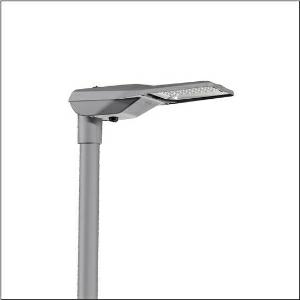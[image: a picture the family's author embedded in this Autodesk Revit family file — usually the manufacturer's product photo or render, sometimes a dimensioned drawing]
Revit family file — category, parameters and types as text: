
# Revit family: streetlight_sl_21_iq_mini___stw1_0a_5xe2e31y08hb_518f
name_source: partatom
category: Lighting Fixtures
units: mm (PartAtom-declared; Revit-internal decimal feet)

## family parameters
Cut with Voids When Loaded = No
Host = Face
Light Source = No
Part Type = Normal
Room Calculation Point = No
Round Connector Dimension = Use Diameter
Shared = No

## types (1)
- --- (1 x LED, 9750 lm, 71 W, 3000K)
    Apparent Load = 71 VA
    CIE Flux Codes = 38 75 98 100 100
    Color Rendering = 70
    Color Temperature = 3000K
    Default Elevation = 1800 mm
    Description = Streetlight SL 21 iQ mini, mast luminaire, primary light control with lens, of PMMA, primary optical cover: cover, of toughened safety glass, transparent, light distribution: STW1.0a, light emission: direct distribution, primary light characteristic: asymmetric, installation type: post-top, side-entry, LED, High Power LED, rated luminous flux: 9.750lm, luminous efficacy: 137lm/W, light colour: 730, colour temperature: 3000K, control gear: iQ-Street Remote, D4i with power reduction, control: pre-setting: logarithmic dimming characteristic, Street-Remote, Auto-Match, Temp-Guard, Lumen-Switch, Night-Set, Smart-Wire, Light-Fading, Desk-Remote (wireless, voltage-free reading and setting of iQ features in the workshop via application-optimized NFC function/RFID function), optimised constant luminous flux control (CLO 2.0), mains connection: 220..240V, AC, 50/60Hz, start of lifetime: 71W, end of service life: 75W, reduction: 30W, luminaire housing, of diecast aluminium, powder-coated, SITECO metallic grey (DB 702S), corrosivity category C5 high according to DIN EN ISO 12944, please order mast flange separately, inclination adjustable: 0°, 5°, 10°, 15°, sealing non-destructively replaceable, multi-level sealing system, length: 628mm, width: 235mm, height: 110mm, mast flange for spigot size: 42mm (side-entry): 5XC10008XM4, 60/48mm (side-entry/post-top): 5XC10108XM2, 76/60mm (side-entry/post-top): 5XC10108XM1, mounting height: 4..8m, Smart Interface below and above, protection rating (complete): IP66, insulation class (complete): insulation class II (safety insulation), certification: CE, ENEC, ENEC+, VDE, impact resistance: IK10, permissible operating ambient temperature for outdoor applications: -40..+50°C, standard-compliant lighting for roads and squares, packaging unit: 1 piece

Light Distribution: STW1.0a
    Height = 110 mm
    Lamp = 1 x LED
    Lamp Light Flux = 9750 lm
    Lamp Power = 71 W
    Lamp count = 1
    Length = 625 mm
    Luminous efficacy = 137 lm/W
    Manufacturer = Siteco
    ModVariant = No
    Model = 5XE2E31Y08HB
    Number of Poles = 1
    OnlyDefault = Yes
    Power Factor = 1
    Product Name = Streetlight SL 21 iQ mini | STW1.0a
    Product group = mast luminaire | pylon top
    ProductGroupID = 6100
    Protection Class = Protection class II
    Protection Degree = IP 66
    RLX_Detail_Level = 1
    RLX_Emergency_Light_Flux = 0 lm
    RLX_Emergency_Type = 0
    RLX_Emergency_Type_DB = No
    RlxData = <blob elided: 92701 chars, md5=8c63b040>
    Socket = socket
    Standby Power = 0 W
    System Light Flux = 9750 lm
    System Power = 71 W
    Type Comments = factory setting: luminous flux: 100 % | dim-lin: 254 | 716 mA
    Type Image = l_1003514.jpg
    URL = http://relux.com
    VarID = @adj_114423
    Voltage = 0 V
    Weight = 0.00 kg
    Width = 234 mm

## geometry (parser evidence)
native form markers: Blend x4, Sweep x10
no freeform markers — native parametric forms only
